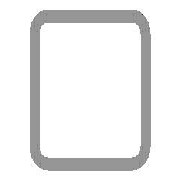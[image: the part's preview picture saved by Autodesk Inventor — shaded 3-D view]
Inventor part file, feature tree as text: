
AUTODESK INVENTOR PART (.ipt)
format: ipt  version: 2025 (Build 290162010, 162A)  size: 133,120 bytes
history: native  units: mm (DEFAULTED — no unit token found)
features: other x4, sketch x1, plane x1
ambient origin geometry x8: Origin, YZ Plane, XZ Plane, XY Plane, X Axis, Y Axis, Z Axis, Center Point
bodies: Solid1 (feature_tree), Body (feature_tree)
feature tree (6):
  parser-record x1  (decoder bookkeeping rows leaked as tree rows — omitted from the tree; the rows remain in map.json)
  other  "Driven Length"
  other  "Start Plane"
  other  "End Plane"
  sketch  "Sketch3"  dims[d3=565.0mm d4=0.0mm d7=4.0mm d9=40.0mm d11=40.0mm d12=2.0mm d13=40.0mm d14=605.0mm d15=20.0mm d16=20.0mm d17=90.0deg d18=565.0mm]
  plane  "Work Plane3"
